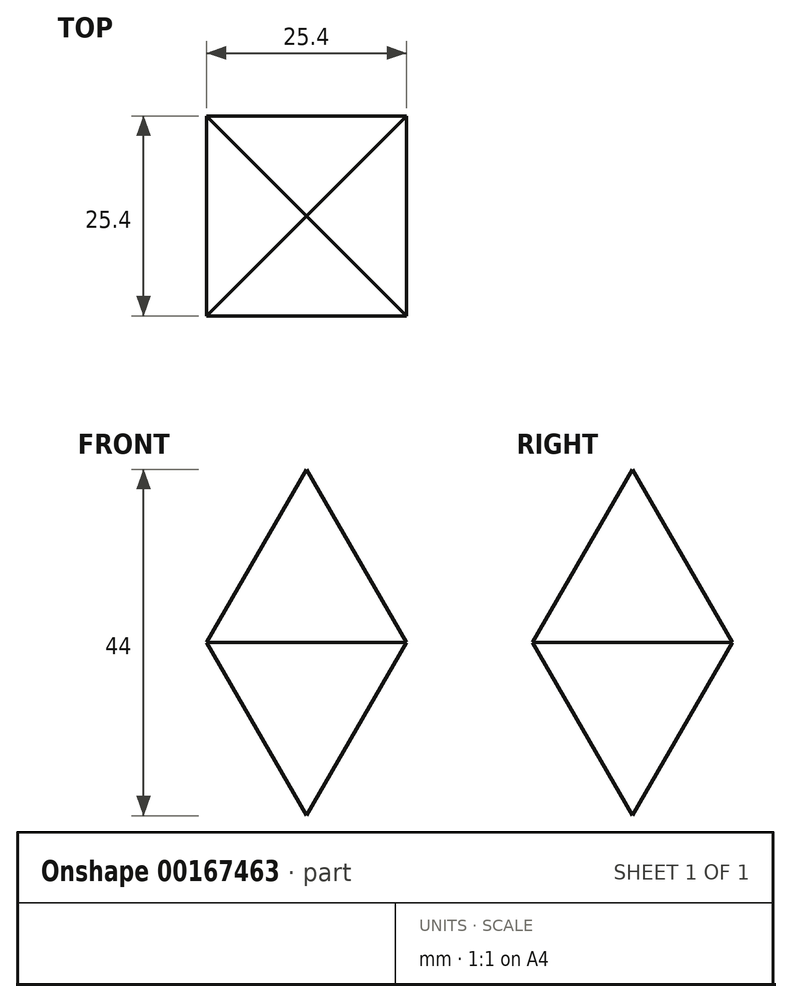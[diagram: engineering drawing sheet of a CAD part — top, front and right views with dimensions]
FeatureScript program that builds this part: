
annotation { "Feature Type Name" : "Feature", "Feature Type Description" : "" }
export const myFeature = defineFeature(function(context is Context, id is Id, definition is map)
    precondition{}
    {
        {
            var Q0;
            Q0=qCreatedBy(makeId("Top.planeOp"),FACE);
            var sketch = newSketch(context, id + "F0", { "sketchPlane" : qUnion([Q0])});
            skLineSegment(sketch, "E0.bottom", {"start": v(12.7, 12.7) * mm, "end": v(-12.7, 12.7) * mm});
            skLineSegment(sketch, "E0.top", {"start": v(12.7, -12.7) * mm, "end": v(-12.7, -12.7) * mm});
            skLineSegment(sketch, "E0.left", {"start": v(12.7, 12.7) * mm, "end": v(12.7, -12.7) * mm});
            skLineSegment(sketch, "E0.right", {"start": v(-12.7, 12.7) * mm, "end": v(-12.7, -12.7) * mm});
            skPoint(sketch, "E0.middle", {"position": v(0, 0) * mm});
            skSolve(sketch);
        }
        {
            var Q0;
            Q0=makeQuery(id+"F0.imprint","IMPRINT",FACE,{"disambiguationData":[TD([[makeQuery(id+"F0.imprint","IMPRINT",EDGE,{"derivedFrom":sQuery(id+"F0.wireOp",EDGE,"E0.bottom")}),1.0]])]});
            extrude(context, id + "F1", {"entities" : qUnion([Q0]), "depth" : 25.4 * mm, "hasDraft" : true, "draftAngle" : 30 * degree, "draftPullDirection" : true, "hasSecondDirection" : true, "secondDirectionOppositeDirection" : true, "secondDirectionDepth" : 25.4 * mm, "hasSecondDirectionDraft" : true, "secondDirectionDraftAngle" : 30 * degree, "secondDirectionDraftPullDirection" : true});
        }
    });
